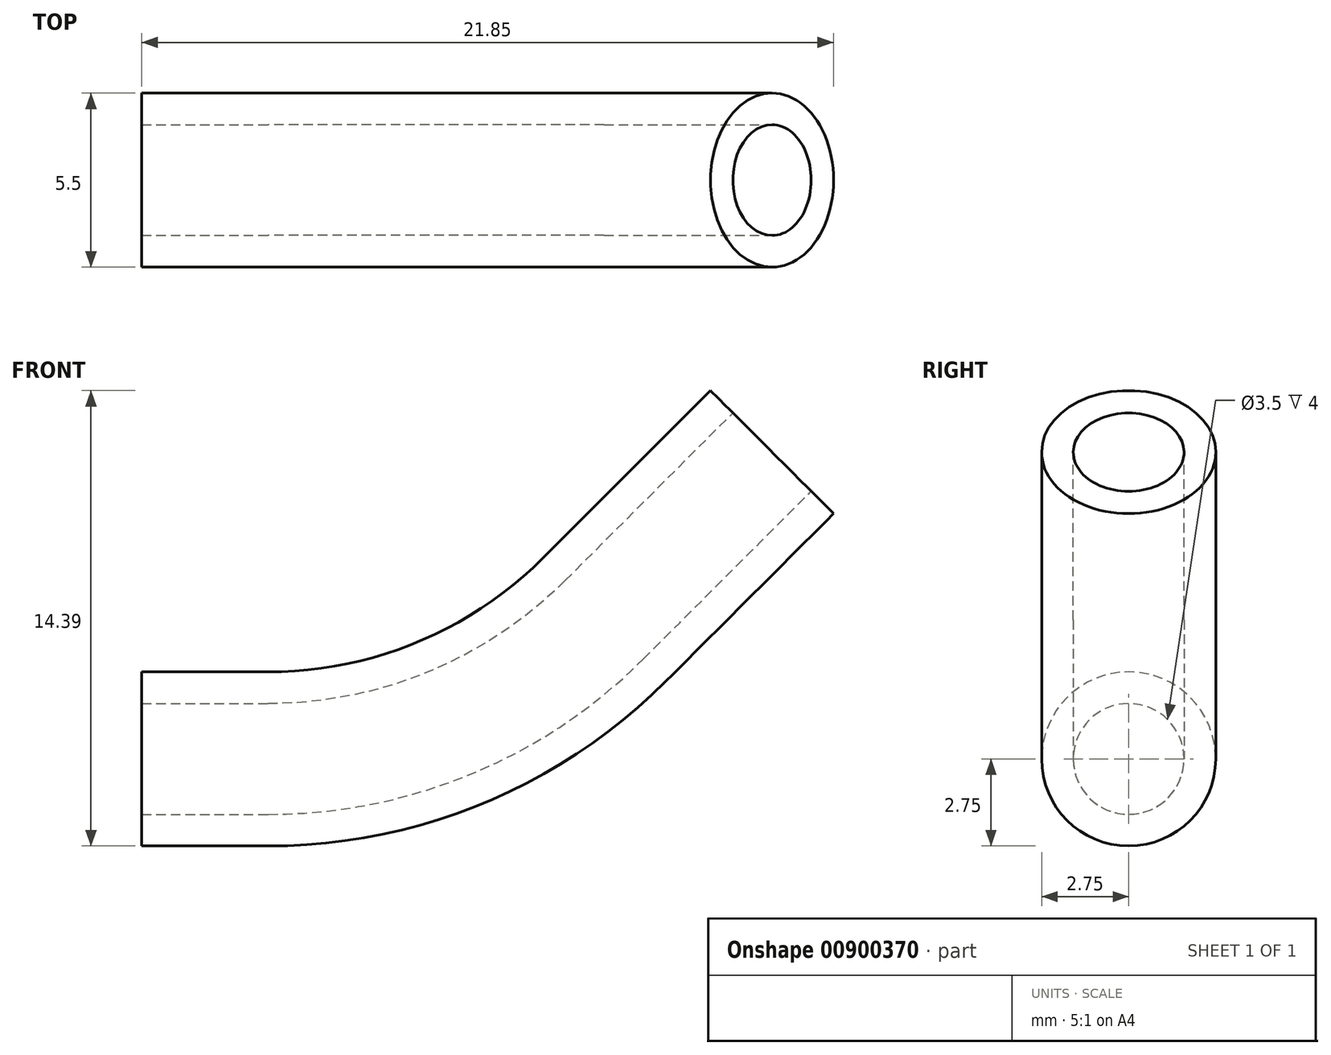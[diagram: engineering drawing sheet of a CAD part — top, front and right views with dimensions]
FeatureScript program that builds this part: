
annotation { "Feature Type Name" : "Feature", "Feature Type Description" : "" }
export const myFeature = defineFeature(function(context is Context, id is Id, definition is map)
    precondition{}
    {
        {
            var Q0;
            Q0=qCreatedBy(makeId("Front.planeOp"),FACE);
            var sketch = newSketch(context, id + "F0", { "sketchPlane" : qUnion([Q0])});
            skLineSegment(sketch, "E0", {"start": v(0, 0) * mm, "end": v(4, 0) * mm});
            skLineSegment(sketch, "E1", {"start": v(14.6, 4.4) * mm, "end": v(19.9, 9.7) * mm});
            skPoint(sketch, "E2.visualSharp", {"position": v(10.21, 0) * mm});
            skArc(sketch, "E2.filletArc", {"start": v(4, 0) * mm, "mid": v(9.74, 1.14) * mm, "end": v(14.6, 4.4) * mm});
            skSolve(sketch);
        }
        {
            var Q0;
            Q0=qCreatedBy(makeId("Right.planeOp"),FACE);
            var sketch = newSketch(context, id + "F1", { "sketchPlane" : qUnion([Q0])});
            skCircle(sketch, "E3", {"center": v(0, 0) * mm, "radius": 2.75 * mm});
            skCircle(sketch, "E4", {"center": v(0, 0) * mm, "radius": 1.75 * mm});
            skSolve(sketch);
        }
        {
            var Q0;
            Q0=makeQuery(id+"F1.imprint","IMPRINT",FACE,{"disambiguationData":[TD([[makeQuery(id+"F1.imprint","IMPRINT",EDGE,{"derivedFrom":sQuery(id+"F1.wireOp",EDGE,"E3")}),1.0]])]});
            var Q1;
            Q1 = qConstructionFilter(qBodyType(qCreatedBy(id + "F0" ,EDGE), BodyType.WIRE), ConstructionObject.NO);
            sweep(context, id + "F2", {"profiles" : qUnion([Q0]), "path" : qUnion([Q1])});
        }
    });
